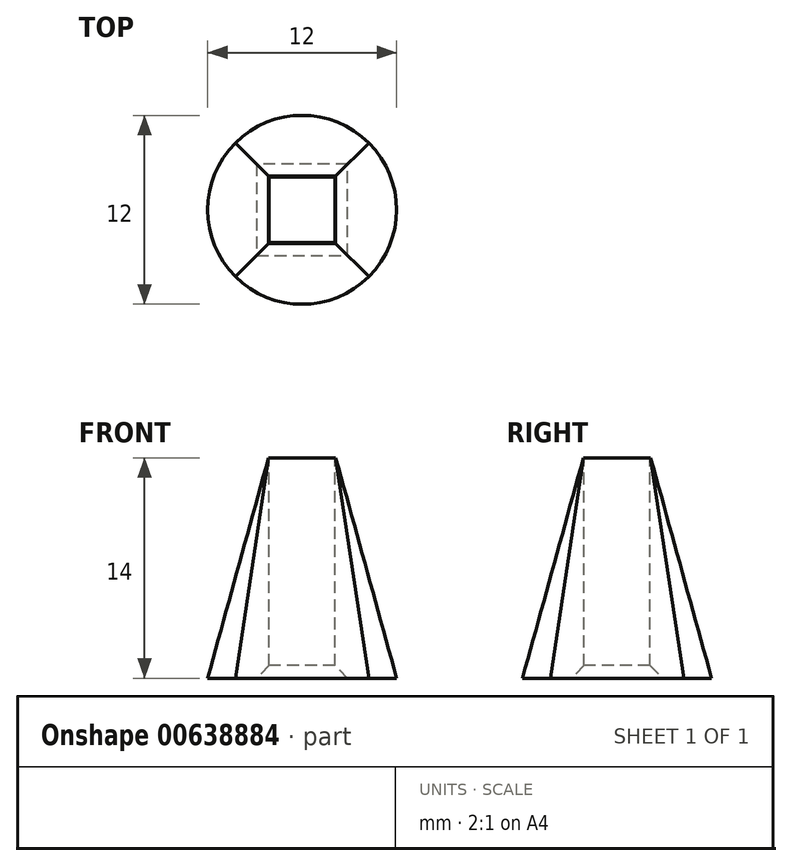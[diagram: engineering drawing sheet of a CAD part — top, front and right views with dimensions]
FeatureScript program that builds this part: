
annotation { "Feature Type Name" : "Feature", "Feature Type Description" : "" }
export const myFeature = defineFeature(function(context is Context, id is Id, definition is map)
    precondition{}
    {
        {
            var Q0;
            Q0=qCreatedBy(makeId("Top.planeOp"),FACE);
            var sketch = newSketch(context, id + "F0", { "sketchPlane" : qUnion([Q0])});
            skCircle(sketch, "E0", {"center": v(0, 0) * mm, "radius": 6 * mm});
            skCircle(sketch, "E1", {"center": v(0, 0) * mm, "radius": 3 * mm, "construction": true});
            skSolve(sketch);
        }
        {
            var Q0;
            Q0=makeQuery(id+"F0.imprint","IMPRINT",FACE,{"disambiguationData":[TD([[makeQuery(id+"F0.imprint","IMPRINT",EDGE,{"derivedFrom":sQuery(id+"F0.wireOp",EDGE,"E0")}),1.0]])]});
            cPlane(context, id + "F1", {"entities" : qUnion([Q0]), "cplaneType" : CPlaneType.OFFSET, "offset" : 14 * mm, "width" : 150 * mm, "height" : 150 * mm});
        }
        {
            var Q0;
            Q0=qCreatedBy(id+"F1.planeOp",FACE);
            var sketch = newSketch(context, id + "F2", { "sketchPlane" : qUnion([Q0])});
            skLineSegment(sketch, "E2.bottom", {"start": v(2.13, -2.13) * mm, "end": v(-2.13, -2.14) * mm});
            skLineSegment(sketch, "E2.top", {"start": v(2.13, 2.14) * mm, "end": v(-2.13, 2.14) * mm});
            skLineSegment(sketch, "E2.left", {"start": v(2.13, -2.13) * mm, "end": v(2.13, 2.14) * mm});
            skLineSegment(sketch, "E2.right", {"start": v(-2.13, -2.14) * mm, "end": v(-2.13, 2.14) * mm});
            skPoint(sketch, "E2.middle", {"position": v(0, 0) * mm});
            skSolve(sketch);
        }
        {
            var Q0;
            Q0=makeQuery(id+"F0.imprint","IMPRINT",FACE,{"disambiguationData":[TD([[makeQuery(id+"F0.imprint","IMPRINT",EDGE,{"derivedFrom":sQuery(id+"F0.wireOp",EDGE,"E0")}),1.0]])]});
            var Q1;
            Q1=makeQuery(id+"F2.imprint","IMPRINT",FACE,{"disambiguationData":[TD([[makeQuery(id+"F2.imprint","IMPRINT",EDGE,{"derivedFrom":sQuery(id+"F2.wireOp",EDGE,"E2.bottom")}),-1.0]])]});
            loft(context, id + "F3", {"sheetProfilesArray" : [{ "sheetProfileEntities" : qUnion([Q0]) }, { "sheetProfileEntities" : qUnion([Q1]) }]});
        }
        {
            var Q0;
            Q0=makeQuery(id+"F3.opLoft","CAP_FACE",FACE,{"disambiguationData":[OSD([makeQuery(id+"F2.imprint","IMPRINT",FACE,{"disambiguationData":[TD([[makeQuery(id+"F2.imprint","IMPRINT",EDGE,{"derivedFrom":sQuery(id+"F2.wireOp",EDGE,"E2.bottom")}),-1.0]])]})])],"isStart":true});
            var sketch = newSketch(context, id + "F4", { "sketchPlane" : qUnion([Q0])});
            skLineSegment(sketch, "E3.bottom", {"start": v(2.09, -2.1) * mm, "end": v(-2.09, -2.1) * mm});
            skLineSegment(sketch, "E3.top", {"start": v(2.09, 2.1) * mm, "end": v(-2.09, 2.09) * mm});
            skLineSegment(sketch, "E3.left", {"start": v(2.09, -2.1) * mm, "end": v(2.09, 2.1) * mm});
            skLineSegment(sketch, "E3.right", {"start": v(-2.09, -2.1) * mm, "end": v(-2.09, 2.09) * mm});
            skPoint(sketch, "E3.middle", {"position": v(0, 0) * mm});
            skSolve(sketch);
        }
        {
            var Q0;
            Q0=makeQuery(id+"F4.imprint","IMPRINT",FACE,{"disambiguationData":[TD([[makeQuery(id+"F4.imprint","IMPRINT",EDGE,{"derivedFrom":sQuery(id+"F4.wireOp",EDGE,"E3.bottom")}),-1.0]])]});
            extrude(context, id + "F5", {"entities" : qUnion([Q0]), "operationType" : NewBodyOperationType.REMOVE, "oppositeDirection" : true, "depth" : 25 * mm, "offsetDistance" : 25 * mm});
        }
        {
            var Q0;
            Q0=makeQuery(id+"F5.boolean.opBoolean","INTERSECT",EDGE,{"derivedFrom":[makeQuery(id+"F3.opLoft","CAP_FACE",FACE,{"disambiguationData":[OSD([makeQuery(id+"F0.imprint","IMPRINT",FACE,{"disambiguationData":[TD([[makeQuery(id+"F0.imprint","IMPRINT",EDGE,{"derivedFrom":sQuery(id+"F0.wireOp",EDGE,"E0")}),1.0]])]})])],"isStart":true}),makeQuery(id+"F5.opExtrude","SWEPT_FACE",FACE,{"disambiguationData":[OSD([sQuery(id+"F4.wireOp",EDGE,"E3.right")])]})]});
            var Q1;
            Q1=makeQuery(id+"F5.boolean.opBoolean","INTERSECT",EDGE,{"derivedFrom":[makeQuery(id+"F3.opLoft","CAP_FACE",FACE,{"disambiguationData":[OSD([makeQuery(id+"F0.imprint","IMPRINT",FACE,{"disambiguationData":[TD([[makeQuery(id+"F0.imprint","IMPRINT",EDGE,{"derivedFrom":sQuery(id+"F0.wireOp",EDGE,"E0")}),1.0]])]})])],"isStart":true}),makeQuery(id+"F5.opExtrude","SWEPT_FACE",FACE,{"disambiguationData":[OSD([sQuery(id+"F4.wireOp",EDGE,"E3.bottom")])]})]});
            var Q2;
            Q2=makeQuery(id+"F5.boolean.opBoolean","INTERSECT",EDGE,{"derivedFrom":[makeQuery(id+"F3.opLoft","CAP_FACE",FACE,{"disambiguationData":[OSD([makeQuery(id+"F0.imprint","IMPRINT",FACE,{"disambiguationData":[TD([[makeQuery(id+"F0.imprint","IMPRINT",EDGE,{"derivedFrom":sQuery(id+"F0.wireOp",EDGE,"E0")}),1.0]])]})])],"isStart":true}),makeQuery(id+"F5.opExtrude","SWEPT_FACE",FACE,{"disambiguationData":[OSD([sQuery(id+"F4.wireOp",EDGE,"E3.left")])]})]});
            var Q3;
            Q3=makeQuery(id+"F5.boolean.opBoolean","INTERSECT",EDGE,{"derivedFrom":[makeQuery(id+"F3.opLoft","CAP_FACE",FACE,{"disambiguationData":[OSD([makeQuery(id+"F0.imprint","IMPRINT",FACE,{"disambiguationData":[TD([[makeQuery(id+"F0.imprint","IMPRINT",EDGE,{"derivedFrom":sQuery(id+"F0.wireOp",EDGE,"E0")}),1.0]])]})])],"isStart":true}),makeQuery(id+"F5.opExtrude","SWEPT_FACE",FACE,{"disambiguationData":[OSD([sQuery(id+"F4.wireOp",EDGE,"E3.top")])]})]});
            chamfer(context, id + "F6", {"entities" : qUnion([Q0, Q1, Q2, Q3]), "chamferType" : ChamferType.OFFSET_ANGLE, "width" : .8 * mm, "oppositeDirection" : false, "angle" : 45 * degree, "tangentPropagation" : true});
        }
    });
